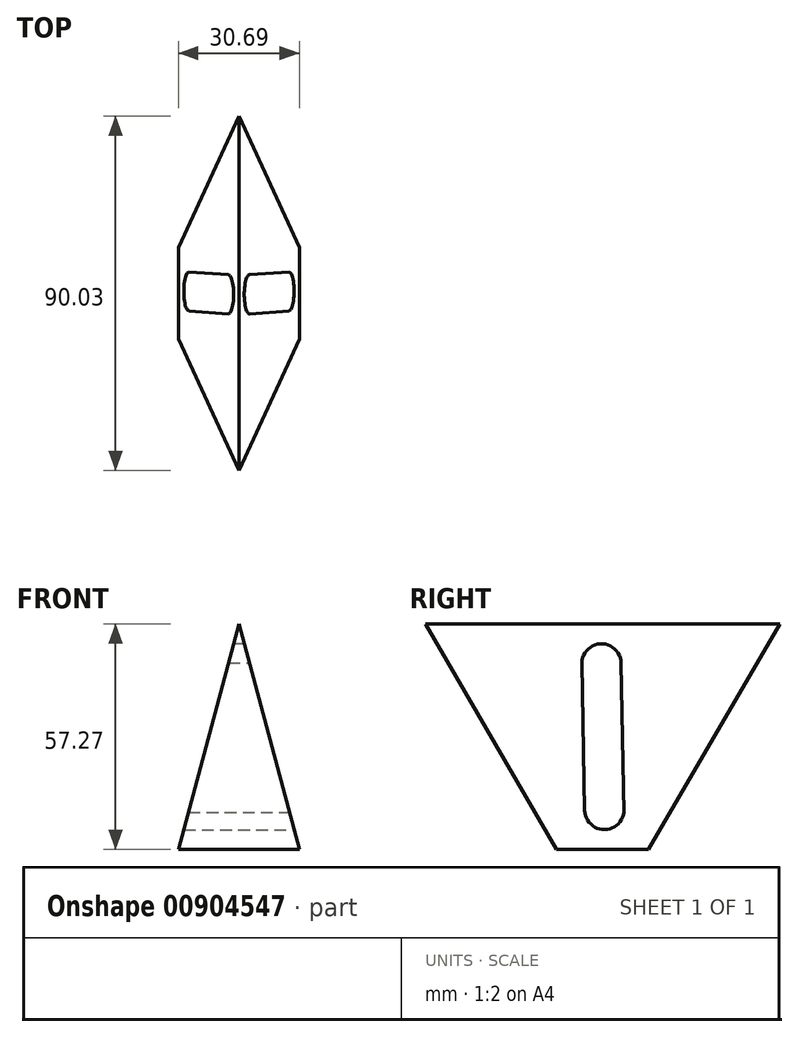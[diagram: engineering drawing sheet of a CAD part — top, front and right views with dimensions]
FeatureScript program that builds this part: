
annotation { "Feature Type Name" : "Feature", "Feature Type Description" : "" }
export const myFeature = defineFeature(function(context is Context, id is Id, definition is map)
    precondition{}
    {
        {
            var Q0;
            Q0=qCreatedBy(makeId("Front.planeOp"),FACE);
            var sketch = newSketch(context, id + "F0", { "sketchPlane" : qUnion([Q0])});
            skLineSegment(sketch, "E0", {"start": v(0, 0) * mm, "end": v(-41.41, 0) * mm});
            skLineSegment(sketch, "E1", {"start": v(-41.41, 0) * mm, "end": v(-20.7, 77.27) * mm});
            skLineSegment(sketch, "E2", {"start": v(0, 0) * mm, "end": v(-20.7, 77.27) * mm});
            skSolve(sketch);
        }
        {
            var Q0;
            Q0=makeQuery(id+"F0.imprint","IMPRINT",FACE,{"disambiguationData":[TD([[makeQuery(id+"F0.imprint","IMPRINT",EDGE,{"derivedFrom":sQuery(id+"F0.wireOp",EDGE,"E0")}),-1.0]])]});
            extrude(context, id + "F1", {"entities" : qUnion([Q0]), "depth" : 90.03 * mm, "offsetDistance" : 25 * mm});
        }
        {
            var Q0;
            Q0=qCreatedBy(makeId("Right.planeOp"),FACE);
            var sketch = newSketch(context, id + "F2", { "sketchPlane" : qUnion([Q0])});
            skLineSegment(sketch, "E3", {"start": v(0, 0) * mm, "end": v(-90.03, 0) * mm});
            skLineSegment(sketch, "E4", {"start": v(-90.03, 0) * mm, "end": v(-90.03, 77.27) * mm});
            skLineSegment(sketch, "E5", {"start": v(0, 0) * mm, "end": v(0, 77.27) * mm});
            skLineSegment(sketch, "E6", {"start": v(-56.67, 20) * mm, "end": v(-33.37, 20) * mm});
            skLineSegment(sketch, "E7", {"start": v(-90.03, 77.27) * mm, "end": v(-56.67, 20) * mm});
            skLineSegment(sketch, "E8", {"start": v(-33.37, 20) * mm, "end": v(0, 77.27) * mm});
            skCircle(sketch, "E9", {"center": v(-44.54, 30) * mm, "radius": 5 * mm});
            skCircle(sketch, "E10", {"center": v(-45.27, 67.27) * mm, "radius": 5 * mm});
            skLineSegment(sketch, "E11", {"start": v(-39.57, 29.43) * mm, "end": v(-40.28, 67.37) * mm});
            skLineSegment(sketch, "E12", {"start": v(-40.28, 67.37) * mm, "end": v(-50.27, 67.37) * mm});
            skLineSegment(sketch, "E13", {"start": v(-50.27, 67.37) * mm, "end": v(-49.54, 29.9) * mm});
            skLineSegment(sketch, "E14", {"start": v(-49.54, 29.9) * mm, "end": v(-39.57, 30) * mm});
            skSolve(sketch);
        }
        {
            var Q0;
            Q0=makeQuery(id+"F2.imprint","IMPRINT",FACE,{"disambiguationData":[TD([[makeQuery(id+"F2.imprint","IMPRINT",EDGE,{"derivedFrom":sQuery(id+"F2.wireOp",EDGE,"E3")}),-1.0]])]});
            var Q1;
            {var subQ1=sQuery(id+"F2.wireOp",EDGE,"E9");var subQ3=sQuery(id+"F2.wireOp",EDGE,"E11");var subQ4=makeQuery(id+"F2.imprint","INTERSECT",VERTEX,{"disambiguationData":[OD(1.0)],"derivedFrom":[subQ1,subQ3]});Q1=makeQuery(id+"F2.imprint","IMPRINT",FACE,{"disambiguationData":[TD([[makeQuery(id+"F2.imprint","IMPRINT",EDGE,{"disambiguationData":[TD([[subQ4,-1.0]])],"derivedFrom":subQ1}),-1.0]])]});}
            var Q2;
            {var subQ0=sQuery(id+"F2.wireOp",EDGE,"E11");var subQ1=sQuery(id+"F2.wireOp",EDGE,"E9");var subQ2=makeQuery(id+"F2.imprint","INTERSECT",VERTEX,{"disambiguationData":[OD(0.0)],"derivedFrom":[subQ1,subQ0]});Q2=makeQuery(id+"F2.imprint","IMPRINT",FACE,{"disambiguationData":[TD([[makeQuery(id+"F2.imprint","IMPRINT",EDGE,{"disambiguationData":[TD([[subQ2,-1.0]])],"derivedFrom":subQ0}),1.0]])]});}
            var Q3;
            {var subQ0=sQuery(id+"F2.wireOp",EDGE,"E12");Q3=makeQuery(id+"F2.imprint","IMPRINT",FACE,{"disambiguationData":[TD([[makeQuery(id+"F2.imprint","IMPRINT",EDGE,{"derivedFrom":subQ0}),-1.0]])]});}
            var Q4;
            {var subQ0=sQuery(id+"F2.wireOp",EDGE,"E12");Q4=makeQuery(id+"F2.imprint","IMPRINT",FACE,{"disambiguationData":[TD([[makeQuery(id+"F2.imprint","IMPRINT",EDGE,{"derivedFrom":subQ0}),1.0]])]});}
            var Q5;
            {var subQ1=sQuery(id+"F2.wireOp",EDGE,"E9");var subQ3=sQuery(id+"F2.wireOp",EDGE,"E11");var subQ4=makeQuery(id+"F2.imprint","INTERSECT",VERTEX,{"disambiguationData":[OD(1.0)],"derivedFrom":[subQ1,subQ3]});Q5=makeQuery(id+"F2.imprint","IMPRINT",FACE,{"disambiguationData":[TD([[makeQuery(id+"F2.imprint","IMPRINT",EDGE,{"disambiguationData":[TD([[subQ4,1.0]])],"derivedFrom":subQ3}),1.0]])]});}
            extrude(context, id + "F3", {"entities" : qUnion([Q0, Q1, Q2, Q3, Q4, Q5]), "operationType" : NewBodyOperationType.REMOVE, "oppositeDirection" : true, "depth" : 100 * mm, "offsetDistance" : 25 * mm});
        }
    });
